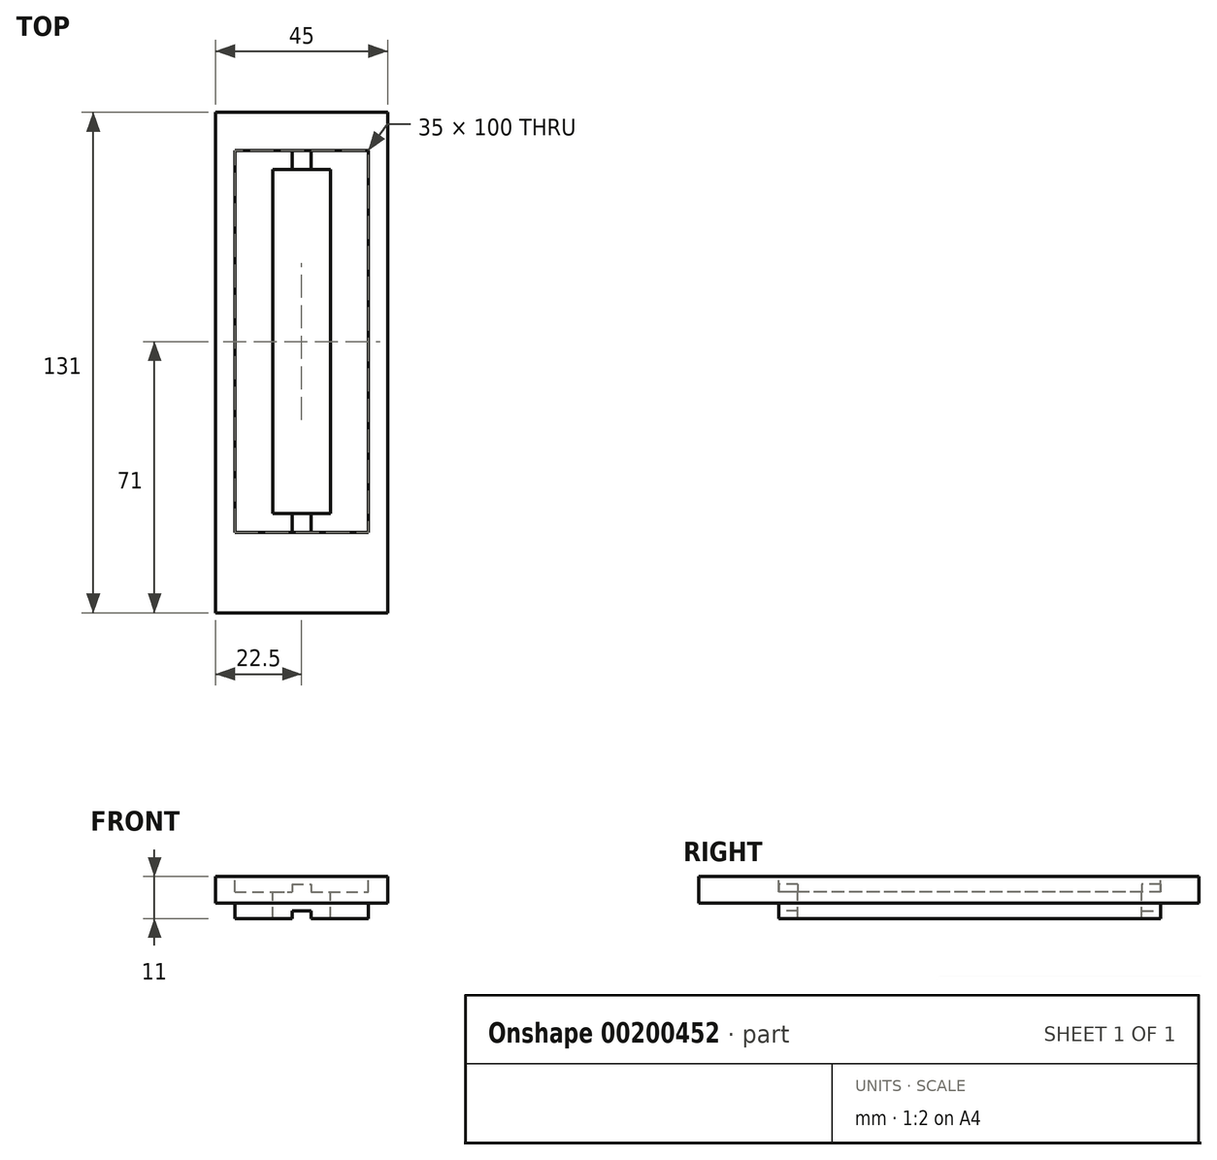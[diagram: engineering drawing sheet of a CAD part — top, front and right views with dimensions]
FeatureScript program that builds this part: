
annotation { "Feature Type Name" : "Feature", "Feature Type Description" : "" }
export const myFeature = defineFeature(function(context is Context, id is Id, definition is map)
    precondition{}
    {
        {
            var Q0;
            Q0=qCreatedBy(makeId("Top.planeOp"),FACE);
            var sketch = newSketch(context, id + "F0", { "sketchPlane" : qUnion([Q0])});
            skLineSegment(sketch, "E0.bottom", {"start": v(0, 0) * mm, "end": v(45, 0) * mm});
            skLineSegment(sketch, "E0.top", {"start": v(0, 131) * mm, "end": v(45, 131) * mm});
            skLineSegment(sketch, "E0.left", {"start": v(0, 0) * mm, "end": v(0, 131) * mm});
            skLineSegment(sketch, "E0.right", {"start": v(45, 0) * mm, "end": v(45, 131) * mm});
            skSolve(sketch);
        }
        {
            var Q0;
            Q0=qSketchRegion(id+"F0",true);
            extrude(context, id + "F1", {"entities" : qUnion([Q0]), "depth" : 2 * mm});
        }
        {
            var Q0;
            Q0=makeQuery(id+"F1.opExtrude","CAP_FACE",FACE,{"disambiguationData":[OSD([sQuery(id+"F0.wireOp",EDGE,"E0.bottom"),sQuery(id+"F0.wireOp",EDGE,"E0.top"),sQuery(id+"F0.wireOp",EDGE,"E0.left"),sQuery(id+"F0.wireOp",EDGE,"E0.right")])],"isStart":false});
            var sketch = newSketch(context, id + "F2", { "sketchPlane" : qUnion([Q0])});
            skLineSegment(sketch, "E1.bottom", {"start": v(0, 0) * mm, "end": v(45, 0) * mm});
            skLineSegment(sketch, "E1.top", {"start": v(0, 131) * mm, "end": v(45, 131) * mm});
            skLineSegment(sketch, "E1.left", {"start": v(0, 0) * mm, "end": v(0, 131) * mm});
            skLineSegment(sketch, "E1.right", {"start": v(45, 0) * mm, "end": v(45, 131) * mm});
            skSolve(sketch);
        }
        {
            var Q0;
            Q0=qSketchRegion(id+"F2",true);
            extrude(context, id + "F3", {"entities" : qUnion([Q0]), "operationType" : NewBodyOperationType.ADD, "depth" : 5 * mm});
        }
        {
            var Q0;
            Q0=makeQuery(id+"F3.opExtrude","CAP_FACE",FACE,{"disambiguationData":[OSD([sQuery(id+"F2.wireOp",EDGE,"E1.bottom"),sQuery(id+"F2.wireOp",EDGE,"E1.top"),sQuery(id+"F2.wireOp",EDGE,"E1.left"),sQuery(id+"F2.wireOp",EDGE,"E1.right")])],"isStart":false});
            var sketch = newSketch(context, id + "F4", { "sketchPlane" : qUnion([Q0])});
            skLineSegment(sketch, "E2.bottom", {"start": v(15, 116) * mm, "end": v(30, 116) * mm});
            skLineSegment(sketch, "E2.top", {"start": v(15, 26) * mm, "end": v(30, 26) * mm});
            skLineSegment(sketch, "E2.left", {"start": v(15, 116) * mm, "end": v(15, 26) * mm});
            skLineSegment(sketch, "E2.right", {"start": v(30, 116) * mm, "end": v(30, 26) * mm});
            skSolve(sketch);
        }
        {
            var Q0;
            Q0=makeQuery(id+"F3.opExtrude","CAP_FACE",FACE,{"disambiguationData":[OSD([sQuery(id+"F2.wireOp",EDGE,"E1.bottom"),sQuery(id+"F2.wireOp",EDGE,"E1.top"),sQuery(id+"F2.wireOp",EDGE,"E1.left"),sQuery(id+"F2.wireOp",EDGE,"E1.right")])],"isStart":false});
            var sketch = newSketch(context, id + "F5", { "sketchPlane" : qUnion([Q0])});
            skLineSegment(sketch, "E3.bottom", {"start": v(5, 121) * mm, "end": v(40, 121) * mm});
            skLineSegment(sketch, "E3.top", {"start": v(5, 21) * mm, "end": v(40, 21) * mm});
            skLineSegment(sketch, "E3.left", {"start": v(5, 121) * mm, "end": v(5, 21) * mm});
            skLineSegment(sketch, "E3.right", {"start": v(40, 121) * mm, "end": v(40, 21) * mm});
            skSolve(sketch);
        }
        {
            var Q0;
            Q0=qSketchRegion(id+"F5",true);
            extrude(context, id + "F6", {"entities" : qUnion([Q0]), "operationType" : NewBodyOperationType.REMOVE, "oppositeDirection" : true, "depth" : 4 * mm});
        }
        {
            var Q0;
            Q0=makeQuery(id+"F6.boolean.opBoolean","COPY",FACE,{"derivedFrom":makeQuery(id+"F6.opExtrude","CAP_FACE",FACE,{"disambiguationData":[OSD([sQuery(id+"F5.wireOp",EDGE,"E3.bottom"),sQuery(id+"F5.wireOp",EDGE,"E3.top"),sQuery(id+"F5.wireOp",EDGE,"E3.left"),sQuery(id+"F5.wireOp",EDGE,"E3.right")])],"isStart":false})});
            var sketch = newSketch(context, id + "F7", { "sketchPlane" : qUnion([Q0])});
            skLineSegment(sketch, "E4.bottom", {"start": v(20, 121) * mm, "end": v(25, 121) * mm});
            skLineSegment(sketch, "E4.top", {"start": v(20, 21) * mm, "end": v(25, 21) * mm});
            skLineSegment(sketch, "E4.left", {"start": v(20, 121) * mm, "end": v(20, 21) * mm});
            skLineSegment(sketch, "E4.right", {"start": v(25, 121) * mm, "end": v(25, 21) * mm});
            skSolve(sketch);
        }
        {
            var Q0;
            Q0=qSketchRegion(id+"F7",true);
            extrude(context, id + "F8", {"entities" : qUnion([Q0]), "operationType" : NewBodyOperationType.ADD, "depth" : 2 * mm});
        }
        {
            var Q0;
            Q0=qSketchRegion(id+"F4",true);
            extrude(context, id + "F9", {"entities" : qUnion([Q0]), "operationType" : NewBodyOperationType.REMOVE, "endBound" : BoundingType.THROUGH_ALL, "oppositeDirection" : true, "depth" : 25.4 * mm});
        }
        {
            var Q0;
            Q0=makeQuery(id+"F1.opExtrude","CAP_FACE",FACE,{"disambiguationData":[OSD([sQuery(id+"F0.wireOp",EDGE,"E0.bottom"),sQuery(id+"F0.wireOp",EDGE,"E0.top"),sQuery(id+"F0.wireOp",EDGE,"E0.left"),sQuery(id+"F0.wireOp",EDGE,"E0.right")])],"isStart":true});
            var sketch = newSketch(context, id + "F10", { "sketchPlane" : qUnion([Q0])});
            skLineSegment(sketch, "E5.bottom", {"start": v(20, -116) * mm, "end": v(25, -116) * mm});
            skLineSegment(sketch, "E5.top", {"start": v(20, -121) * mm, "end": v(25, -121) * mm});
            skLineSegment(sketch, "E5.left", {"start": v(20, -116) * mm, "end": v(20, -121) * mm});
            skLineSegment(sketch, "E5.right", {"start": v(25, -116) * mm, "end": v(25, -121) * mm});
            skPoint(sketch, "E6.firstSnap0", {"position": v(22.5, -26) * mm});
            skLineSegment(sketch, "E6.bottom", {"start": v(25, -26) * mm, "end": v(20, -26) * mm});
            skLineSegment(sketch, "E6.top", {"start": v(25, -21) * mm, "end": v(20, -21) * mm});
            skLineSegment(sketch, "E6.left", {"start": v(25, -26) * mm, "end": v(25, -21) * mm});
            skLineSegment(sketch, "E6.right", {"start": v(20, -26) * mm, "end": v(20, -21) * mm});
            skSolve(sketch);
        }
        {
            var Q0;
            Q0=makeQuery(id+"F10.imprint","IMPRINT",FACE,{"disambiguationData":[TD([[makeQuery(id+"F10.imprint","IMPRINT",EDGE,{"derivedFrom":sQuery(id+"F10.wireOp",EDGE,"E5.top")}),-1.0]])]});
            var sketch = newSketch(context, id + "F11", { "sketchPlane" : qUnion([Q0])});
            skLineSegment(sketch, "E7.bottom", {"start": v(5, -21) * mm, "end": v(15, -21) * mm});
            skLineSegment(sketch, "E7.top", {"start": v(5, -121) * mm, "end": v(15, -121) * mm});
            skLineSegment(sketch, "E7.left", {"start": v(5, -21) * mm, "end": v(5, -121) * mm});
            skLineSegment(sketch, "E7.right", {"start": v(15, -21) * mm, "end": v(15, -121) * mm});
            skLineSegment(sketch, "E8.bottom", {"start": v(30, -21) * mm, "end": v(40, -21) * mm});
            skLineSegment(sketch, "E8.top", {"start": v(30, -121) * mm, "end": v(40, -121) * mm});
            skLineSegment(sketch, "E8.left", {"start": v(30, -21) * mm, "end": v(30, -121) * mm});
            skLineSegment(sketch, "E8.right", {"start": v(40, -21) * mm, "end": v(40, -121) * mm});
            skSolve(sketch);
        }
        {
            var Q0;
            Q0=makeQuery(id+"F10.imprint","IMPRINT",FACE,{"disambiguationData":[TD([[makeQuery(id+"F10.imprint","IMPRINT",EDGE,{"derivedFrom":sQuery(id+"F10.wireOp",EDGE,"E5.top")}),-1.0]])]});
            var sketch = newSketch(context, id + "F12", { "sketchPlane" : qUnion([Q0])});
            skLineSegment(sketch, "E9.bottom", {"start": v(15, -21) * mm, "end": v(20, -21) * mm});
            skLineSegment(sketch, "E9.top", {"start": v(15, -26) * mm, "end": v(20, -26) * mm});
            skLineSegment(sketch, "E9.left", {"start": v(15, -21) * mm, "end": v(15, -26) * mm});
            skLineSegment(sketch, "E9.right", {"start": v(20, -21) * mm, "end": v(20, -26) * mm});
            skLineSegment(sketch, "E10.bottom", {"start": v(25, -21) * mm, "end": v(30, -21) * mm});
            skLineSegment(sketch, "E10.top", {"start": v(25, -26) * mm, "end": v(30, -26) * mm});
            skLineSegment(sketch, "E10.left", {"start": v(25, -21) * mm, "end": v(25, -26) * mm});
            skLineSegment(sketch, "E10.right", {"start": v(30, -21) * mm, "end": v(30, -26) * mm});
            skLineSegment(sketch, "E11.bottom", {"start": v(25, -116) * mm, "end": v(30, -116) * mm});
            skLineSegment(sketch, "E11.top", {"start": v(25, -121) * mm, "end": v(30, -121) * mm});
            skLineSegment(sketch, "E11.left", {"start": v(25, -116) * mm, "end": v(25, -121) * mm});
            skLineSegment(sketch, "E11.right", {"start": v(30, -116) * mm, "end": v(30, -121) * mm});
            skLineSegment(sketch, "E12.bottom", {"start": v(15, -116) * mm, "end": v(20, -116) * mm});
            skLineSegment(sketch, "E12.top", {"start": v(15, -121) * mm, "end": v(20, -121) * mm});
            skLineSegment(sketch, "E12.left", {"start": v(15, -116) * mm, "end": v(15, -121) * mm});
            skLineSegment(sketch, "E12.right", {"start": v(20, -116) * mm, "end": v(20, -121) * mm});
            skSolve(sketch);
        }
        {
            var Q0;
            Q0=qSketchRegion(id+"F10",true);
            extrude(context, id + "F13", {"entities" : qUnion([Q0]), "operationType" : NewBodyOperationType.ADD, "depth" : 2 * mm});
        }
        {
            var Q0;
            Q0=qSketchRegion(id+"F12",true);
            extrude(context, id + "F14", {"entities" : qUnion([Q0]), "operationType" : NewBodyOperationType.ADD, "depth" : 4 * mm});
        }
        {
            var Q0;
            Q0=qSketchRegion(id+"F11",true);
            extrude(context, id + "F15", {"entities" : qUnion([Q0]), "operationType" : NewBodyOperationType.ADD, "depth" : 4 * mm});
        }
    });
